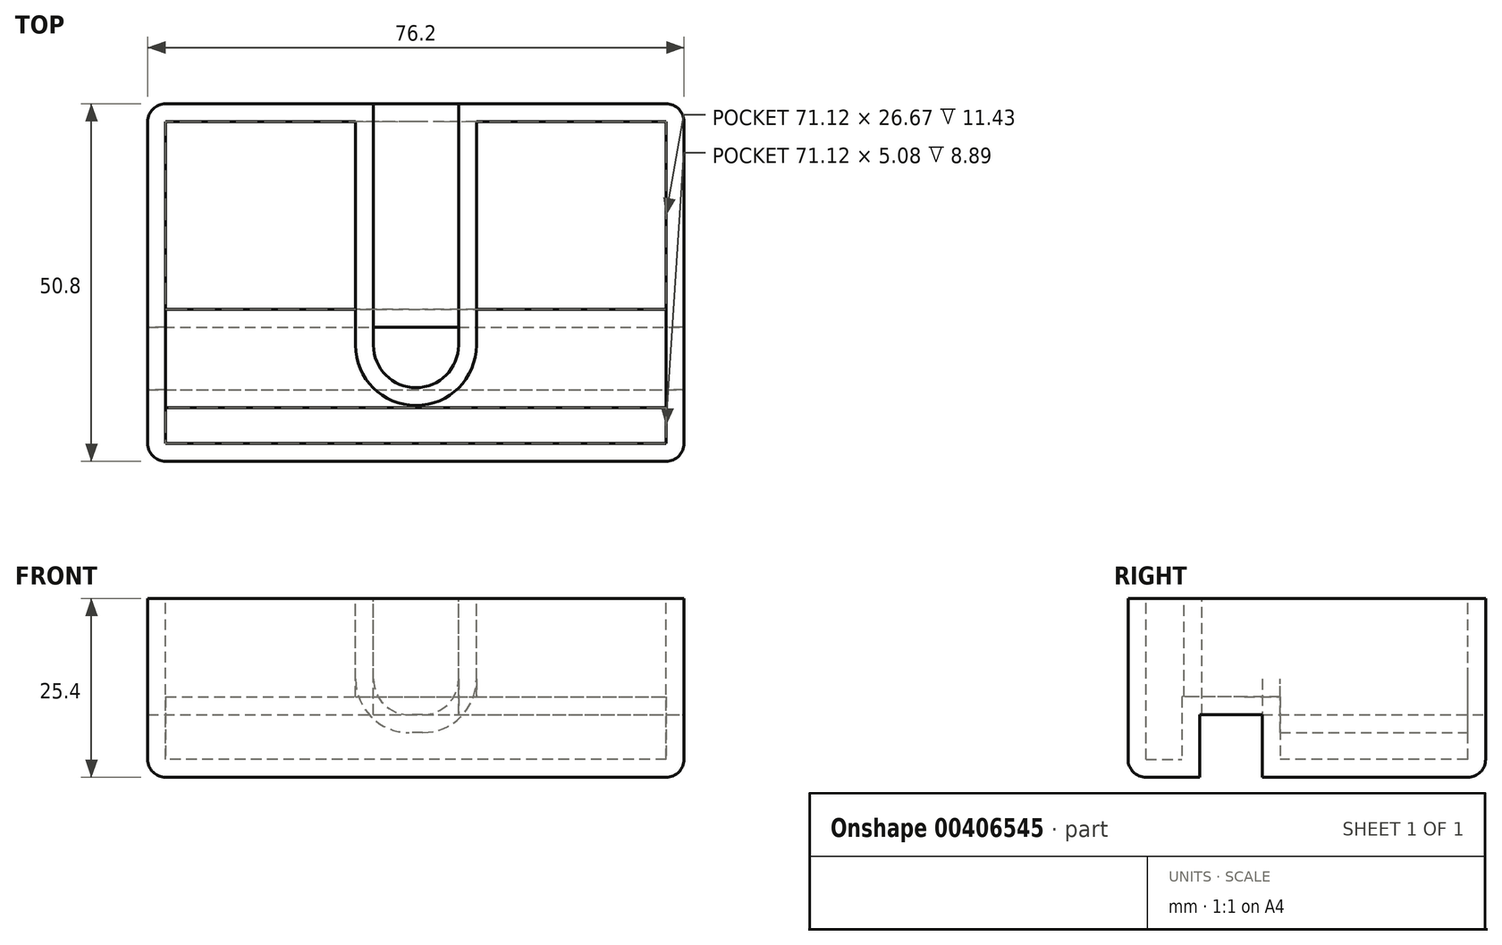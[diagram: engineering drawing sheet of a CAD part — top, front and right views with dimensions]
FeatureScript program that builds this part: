
annotation { "Feature Type Name" : "Feature", "Feature Type Description" : "" }
export const myFeature = defineFeature(function(context is Context, id is Id, definition is map)
    precondition{}
    {
        {
            var Q0;
            Q0=qCreatedBy(makeId("Top.planeOp"),FACE);
            var sketch = newSketch(context, id + "F0", { "sketchPlane" : qUnion([Q0])});
            skLineSegment(sketch, "E0.bottom", {"start": v(-38.1, 25.4) * mm, "end": v(38.1, 25.4) * mm});
            skLineSegment(sketch, "E0.top", {"start": v(-38.1, -25.4) * mm, "end": v(38.1, -25.4) * mm});
            skLineSegment(sketch, "E0.left", {"start": v(-38.1, 25.4) * mm, "end": v(-38.1, -25.4) * mm});
            skLineSegment(sketch, "E0.right", {"start": v(38.1, 25.4) * mm, "end": v(38.1, -25.4) * mm});
            skSolve(sketch);
        }
        {
            var Q0;
            Q0=makeQuery(id+"F0.imprint","IMPRINT",FACE,{"disambiguationData":[TD([[makeQuery(id+"F0.imprint","IMPRINT",EDGE,{"derivedFrom":sQuery(id+"F0.wireOp",EDGE,"E0.bottom")}),-1.0]])]});
            var sketch = newSketch(context, id + "F1", { "sketchPlane" : qUnion([Q0])});
            skLineSegment(sketch, "E1", {"start": v(-38.1, -15.24) * mm, "end": v(38.1, -15.24) * mm});
            skLineSegment(sketch, "E2", {"start": v(-38.1, -6.35) * mm, "end": v(38.1, -6.35) * mm});
            skLineSegment(sketch, "E3", {"start": v(-38.1, -6.35) * mm, "end": v(-38.1, -15.24) * mm});
            skLineSegment(sketch, "E4", {"start": v(38.1, -6.35) * mm, "end": v(38.1, -15.24) * mm});
            skSolve(sketch);
        }
        {
            var Q0;
            Q0=makeQuery(id+"F0.imprint","IMPRINT",FACE,{"disambiguationData":[TD([[makeQuery(id+"F0.imprint","IMPRINT",EDGE,{"derivedFrom":sQuery(id+"F0.wireOp",EDGE,"E0.bottom")}),-1.0]])]});
            extrude(context, id + "F2", {"entities" : qUnion([Q0]), "depth" : 25.4 * mm});
        }
        {
            var Q0;
            Q0=makeQuery(id+"F1.imprint","IMPRINT",FACE,{"disambiguationData":[TD([[makeQuery(id+"F1.imprint","IMPRINT",EDGE,{"derivedFrom":sQuery(id+"F1.wireOp",EDGE,"E1")}),1.0]])]});
            extrude(context, id + "F3", {"entities" : qUnion([Q0]), "operationType" : NewBodyOperationType.REMOVE, "depth" : 8.9 * mm});
        }
        {
            var Q0;
            {var subQ0=sQuery(id+"F0.wireOp",EDGE,"E0.bottom");var subQ1=sQuery(id+"F0.wireOp",EDGE,"E0.left");Q0=makeQuery(id+"F3.boolean.opBoolean","SPLIT",EDGE,{"disambiguationData":[TD([makeQuery(id+"F2.opExtrude","SWEPT_FACE",FACE,{"disambiguationData":[OSD([subQ0])]})])],"derivedFrom":makeQuery(id+"F2.opExtrude","CAP_EDGE",EDGE,{"disambiguationData":[OSD([subQ1])],"isStart":true})});}
            var Q1;
            Q1=makeQuery(id+"F2.opExtrude","CAP_EDGE",EDGE,{"disambiguationData":[OSD([sQuery(id+"F0.wireOp",EDGE,"E0.bottom")])],"isStart":true});
            var Q2;
            {var subQ0=sQuery(id+"F0.wireOp",EDGE,"E0.bottom");var subQ1=sQuery(id+"F0.wireOp",EDGE,"E0.right");Q2=makeQuery(id+"F3.boolean.opBoolean","SPLIT",EDGE,{"disambiguationData":[TD([makeQuery(id+"F2.opExtrude","SWEPT_FACE",FACE,{"disambiguationData":[OSD([subQ0])]})])],"derivedFrom":makeQuery(id+"F2.opExtrude","CAP_EDGE",EDGE,{"disambiguationData":[OSD([subQ1])],"isStart":true})});}
            var Q3;
            {var subQ0=sQuery(id+"F0.wireOp",EDGE,"E0.left");var subQ1=sQuery(id+"F0.wireOp",EDGE,"E0.top");Q3=makeQuery(id+"F3.boolean.opBoolean","SPLIT",EDGE,{"disambiguationData":[TD([makeQuery(id+"F2.opExtrude","SWEPT_FACE",FACE,{"disambiguationData":[OSD([subQ1])]})])],"derivedFrom":makeQuery(id+"F2.opExtrude","CAP_EDGE",EDGE,{"disambiguationData":[OSD([subQ0])],"isStart":true})});}
            var Q4;
            Q4=makeQuery(id+"F2.opExtrude","CAP_EDGE",EDGE,{"disambiguationData":[OSD([sQuery(id+"F0.wireOp",EDGE,"E0.top")])],"isStart":true});
            var Q5;
            {var subQ0=sQuery(id+"F0.wireOp",EDGE,"E0.right");var subQ1=sQuery(id+"F0.wireOp",EDGE,"E0.top");Q5=makeQuery(id+"F3.boolean.opBoolean","SPLIT",EDGE,{"disambiguationData":[TD([makeQuery(id+"F2.opExtrude","SWEPT_FACE",FACE,{"disambiguationData":[OSD([subQ1])]})])],"derivedFrom":makeQuery(id+"F2.opExtrude","CAP_EDGE",EDGE,{"disambiguationData":[OSD([subQ0])],"isStart":true})});}
            var Q6;
            Q6=makeQuery(id+"F2.opExtrude","SWEPT_EDGE",EDGE,{"disambiguationData":[OSD([sQuery(id+"F0.wireOp",EDGE,"E0.bottom"),sQuery(id+"F0.wireOp",EDGE,"E0.left")])]});
            var Q7;
            Q7=makeQuery(id+"F2.opExtrude","SWEPT_EDGE",EDGE,{"disambiguationData":[OSD([sQuery(id+"F0.wireOp",EDGE,"E0.top"),sQuery(id+"F0.wireOp",EDGE,"E0.left")])]});
            var Q8;
            Q8=makeQuery(id+"F2.opExtrude","SWEPT_EDGE",EDGE,{"disambiguationData":[OSD([sQuery(id+"F0.wireOp",EDGE,"E0.top"),sQuery(id+"F0.wireOp",EDGE,"E0.right")])]});
            var Q9;
            Q9=makeQuery(id+"F2.opExtrude","SWEPT_EDGE",EDGE,{"disambiguationData":[OSD([sQuery(id+"F0.wireOp",EDGE,"E0.bottom"),sQuery(id+"F0.wireOp",EDGE,"E0.right")])]});
            fillet(context, id + "F4", {"entities" : qUnion([Q0, Q1, Q2, Q3, Q4, Q5, Q6, Q7, Q8, Q9]), "radius" : 2.54 * mm, "tangentPropagation" : true, "allowEdgeOverflow" : false});
        }
        {
            var Q0;
            Q0=makeQuery(id+"F2.opExtrude","CAP_FACE",FACE,{"disambiguationData":[OSD([sQuery(id+"F0.wireOp",EDGE,"E0.bottom"),sQuery(id+"F0.wireOp",EDGE,"E0.top"),sQuery(id+"F0.wireOp",EDGE,"E0.left"),sQuery(id+"F0.wireOp",EDGE,"E0.right")])],"isStart":false});
            var sketch = newSketch(context, id + "F5", { "sketchPlane" : qUnion([Q0])});
            skLineSegment(sketch, "E5.bottom", {"start": v(-6.05, 25.4) * mm, "end": v(6.05, 25.4) * mm});
            skLineSegment(sketch, "E5.top", {"start": v(-6.05, -8.89) * mm, "end": v(6.05, -8.89) * mm});
            skLineSegment(sketch, "E5.left", {"start": v(-6.05, 25.4) * mm, "end": v(-6.05, -8.89) * mm});
            skLineSegment(sketch, "E5.right", {"start": v(6.05, 25.4) * mm, "end": v(6.05, -8.89) * mm});
            skLineSegment(sketch, "E6.0", {"start": v(-38.1, -6.35) * mm, "end": v(-6.05, -6.35) * mm});
            skLineSegment(sketch, "E7.0", {"start": v(-38.1, -15.24) * mm, "end": v(38.1, -15.24) * mm});
            skArc(sketch, "E8", {"start": v(-6.05, -8.89) * mm, "mid": v(0, -14.94) * mm, "end": v(6.05, -8.89) * mm});
            skLineSegment(sketch, "E9.trimOffspring", {"start": v(6.05, -6.35) * mm, "end": v(38.1, -6.35) * mm});
            skSolve(sketch);
        }
        {
            var Q0;
            {var subQ4=sQuery(id+"F5.wireOp",EDGE,"E5.bottom");Q0=makeQuery(id+"F5.imprint","IMPRINT",FACE,{"disambiguationData":[TD([[makeQuery(id+"F5.imprint","IMPRINT",EDGE,{"derivedFrom":subQ4}),-1.0]])]});}
            var Q1;
            Q1=makeQuery(id+"F5.imprint","IMPRINT",FACE,{"disambiguationData":[TD([[makeQuery(id+"F5.imprint","IMPRINT",EDGE,{"derivedFrom":sQuery(id+"F5.wireOp",EDGE,"E5.top")}),-1.0]])]});
            var Q2;
            Q2=makeQuery(id+"F3.boolean.opBoolean","COPY",FACE,{"derivedFrom":makeQuery(id+"F3.opExtrude","CAP_FACE",FACE,{"disambiguationData":[OSD([sQuery(id+"F1.wireOp",EDGE,"E1"),sQuery(id+"F1.wireOp",EDGE,"E2"),sQuery(id+"F1.wireOp",EDGE,"E3"),sQuery(id+"F1.wireOp",EDGE,"E4")])],"isStart":false})});
            extrude(context, id + "F6", {"entities" : qUnion([Q0, Q1]), "operationType" : NewBodyOperationType.REMOVE, "endBound" : BoundingType.UP_TO_SURFACE, "oppositeDirection" : true, "endBoundEntityFace" : qUnion([Q2]), "depth" : 25.4 * mm});
        }
        {
            var Q0;
            {var subQ0=sQuery(id+"F5.wireOp",EDGE,"E5.left");Q0=makeQuery(id+"F6.boolean.opBoolean","COPY",EDGE,{"disambiguationData":[topologyDisambiguationEdgeConnected([makeQuery(id+"F6.opExtrude","CAP_FACE",FACE,{"disambiguationData":[OSD([sQuery(id+"F5.wireOp",EDGE,"E5.bottom"),subQ0,sQuery(id+"F5.wireOp",EDGE,"E5.right"),sQuery(id+"F5.wireOp",EDGE,"E8")])],"isStart":false})])],"derivedFrom":makeQuery(id+"F6.opExtrude","CAP_EDGE",EDGE,{"disambiguationData":[OSD([subQ0])],"isStart":false})});}
            var Q1;
            {var subQ0=sQuery(id+"F5.wireOp",EDGE,"E5.right");Q1=makeQuery(id+"F6.boolean.opBoolean","COPY",EDGE,{"disambiguationData":[topologyDisambiguationEdgeConnected([makeQuery(id+"F6.opExtrude","CAP_FACE",FACE,{"disambiguationData":[OSD([sQuery(id+"F5.wireOp",EDGE,"E5.bottom"),sQuery(id+"F5.wireOp",EDGE,"E5.left"),subQ0,sQuery(id+"F5.wireOp",EDGE,"E8")])],"isStart":false})])],"derivedFrom":makeQuery(id+"F6.opExtrude","CAP_EDGE",EDGE,{"disambiguationData":[OSD([subQ0])],"isStart":false})});}
            fillet(context, id + "F7", {"entities" : qUnion([Q0, Q1]), "radius" : 5.08 * mm, "tangentPropagation" : true, "allowEdgeOverflow" : false});
        }
        {
            var Q0;
            Q0=makeQuery(id+"F2.opExtrude","CAP_FACE",FACE,{"disambiguationData":[OSD([sQuery(id+"F0.wireOp",EDGE,"E0.bottom"),sQuery(id+"F0.wireOp",EDGE,"E0.top"),sQuery(id+"F0.wireOp",EDGE,"E0.left"),sQuery(id+"F0.wireOp",EDGE,"E0.right")])],"isStart":false});
            shell(context, id + "F8", {"entities" : qUnion([Q0]), "thickness" : 2.54 * mm});
        }
    });
